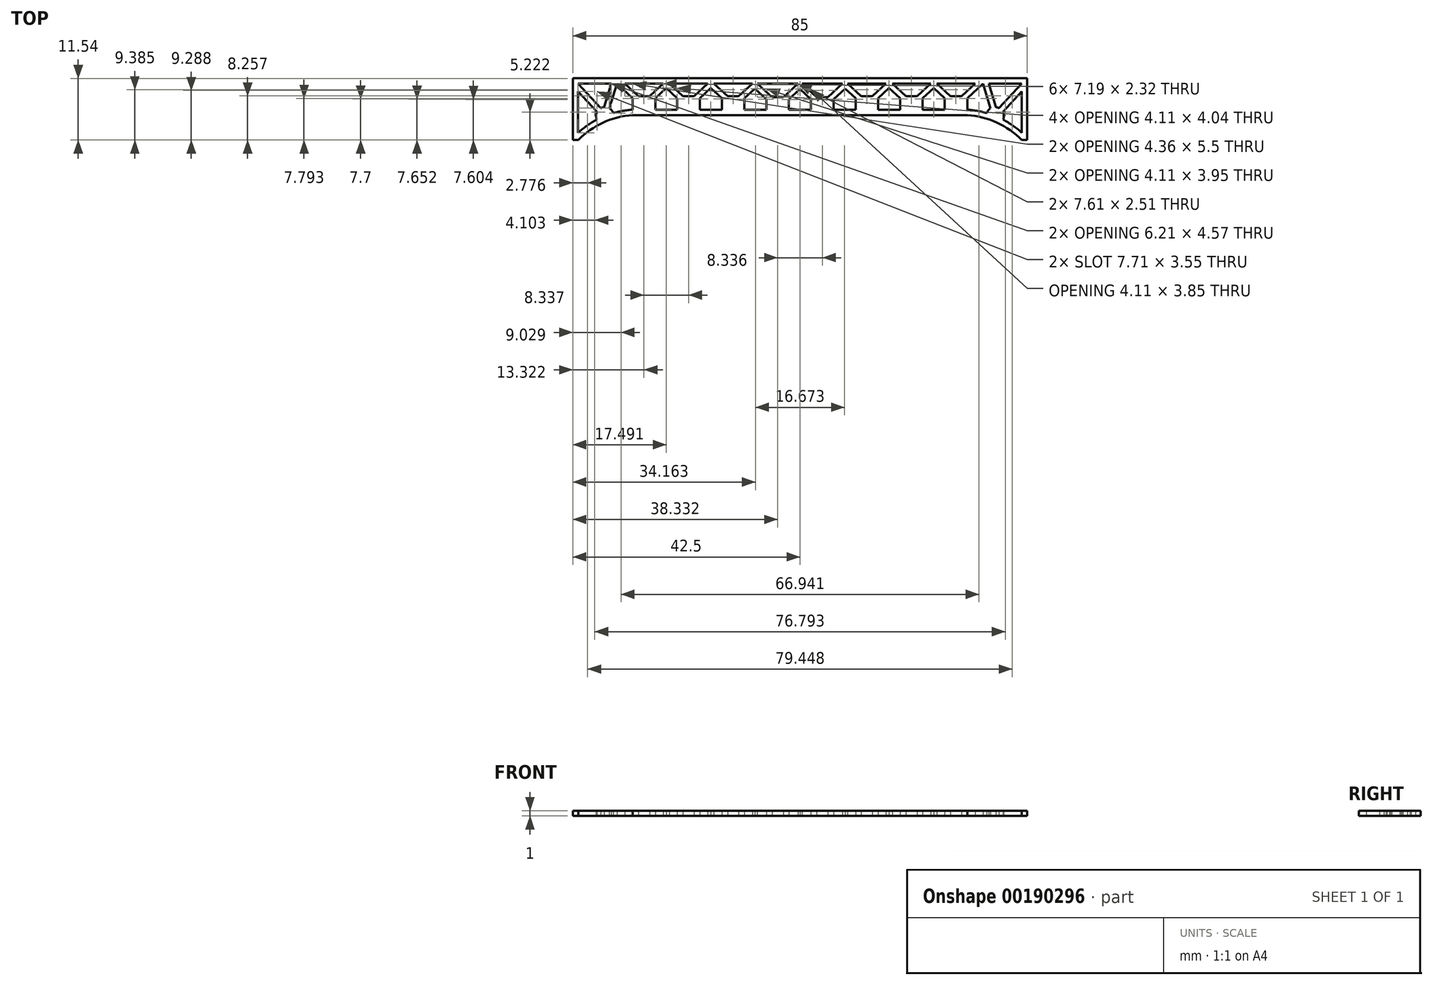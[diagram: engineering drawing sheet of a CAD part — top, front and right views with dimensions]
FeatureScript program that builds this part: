
annotation { "Feature Type Name" : "Feature", "Feature Type Description" : "" }
export const myFeature = defineFeature(function(context is Context, id is Id, definition is map)
    precondition{}
    {
        {
            var Q0;
            Q0=qCreatedBy(makeId("Top.planeOp"),FACE);
            var sketch = newSketch(context, id + "F0", { "sketchPlane" : qUnion([Q0])});
            skLineSegment(sketch, "E0", {"start": v(41.49, -5.77) * mm, "end": v(42.5, -5.77) * mm});
            skLineSegment(sketch, "E1", {"start": v(-28.13, 2.46) * mm, "end": v(-30.22, 2.46) * mm});
            skLineSegment(sketch, "E2", {"start": v(-31.29, -0.1) * mm, "end": v(-31.29, 2.08) * mm});
            skArc(sketch, "E3", {"start": v(41.49, -5.77) * mm, "mid": v(36.82, -2.5) * mm, "end": v(31.29, -1.1) * mm});
            skLineSegment(sketch, "E4", {"start": v(42.5, -5.77) * mm, "end": v(42.5, 5.77) * mm});
            skLineSegment(sketch, "E5", {"start": v(-30.22, 2.46) * mm, "end": v(-32.77, 4.77) * mm});
            skLineSegment(sketch, "E6", {"start": v(-42.5, -5.77) * mm, "end": v(-42.5, 5.77) * mm});
            skArc(sketch, "E7", {"start": v(-31.29, -1.1) * mm, "mid": v(-36.82, -2.5) * mm, "end": v(-41.49, -5.77) * mm});
            skLineSegment(sketch, "E8", {"start": v(-41.49, -5.77) * mm, "end": v(-42.5, -5.77) * mm});
            skLineSegment(sketch, "E9", {"start": v(-42.5, 5.77) * mm, "end": v(42.5, 5.77) * mm});
            skLineSegment(sketch, "E10", {"start": v(-31.29, -1.1) * mm, "end": v(31.29, -1.1) * mm});
            skLineSegment(sketch, "E11", {"start": v(-41.5, 4.77) * mm, "end": v(-35.3, 4.77) * mm});
            skLineSegment(sketch, "E12", {"start": v(-41.5, -4.4) * mm, "end": v(-41.5, 3.3) * mm});
            skArc(sketch, "E13", {"start": v(-31.29, -0.1) * mm, "mid": v(-33.12, -0.3) * mm, "end": v(-34.92, -0.73) * mm});
            skLineSegment(sketch, "E14", {"start": v(-31.29, 2.08) * mm, "end": v(-34.25, 4.77) * mm});
            skLineSegment(sketch, "E15", {"start": v(-27.07, -0.1) * mm, "end": v(-27.07, 2.08) * mm});
            skLineSegment(sketch, "E16", {"start": v(-28.13, 2.46) * mm, "end": v(-25.58, 4.77) * mm});
            skLineSegment(sketch, "E17", {"start": v(-27.07, 2.08) * mm, "end": v(-25, 3.95) * mm});
            skLineSegment(sketch, "E18", {"start": v(-21.89, 2.46) * mm, "end": v(-24.43, 4.77) * mm});
            skLineSegment(sketch, "E19", {"start": v(-18.73, -0.1) * mm, "end": v(-18.73, 2.08) * mm});
            skLineSegment(sketch, "E20", {"start": v(-19.8, 2.46) * mm, "end": v(-21.89, 2.46) * mm});
            skLineSegment(sketch, "E21", {"start": v(-22.95, -0.1) * mm, "end": v(-22.95, 2.08) * mm});
            skLineSegment(sketch, "E22", {"start": v(-19.8, 2.46) * mm, "end": v(-17.25, 4.77) * mm});
            skLineSegment(sketch, "E23", {"start": v(-18.73, 2.08) * mm, "end": v(-16.67, 3.95) * mm});
            skLineSegment(sketch, "E24", {"start": v(-22.95, 2.08) * mm, "end": v(-25, 3.95) * mm});
            skLineSegment(sketch, "E25", {"start": v(-13.55, 2.46) * mm, "end": v(-16.1, 4.77) * mm});
            skLineSegment(sketch, "E26", {"start": v(-10.4, -0.1) * mm, "end": v(-10.4, 2.08) * mm});
            skLineSegment(sketch, "E27", {"start": v(-11.46, 2.46) * mm, "end": v(-13.55, 2.46) * mm});
            skLineSegment(sketch, "E28", {"start": v(-14.62, -0.1) * mm, "end": v(-14.62, 2.08) * mm});
            skLineSegment(sketch, "E29", {"start": v(-11.46, 2.46) * mm, "end": v(-8.91, 4.77) * mm});
            skLineSegment(sketch, "E30", {"start": v(-10.4, 2.08) * mm, "end": v(-8.44, 3.85) * mm});
            skLineSegment(sketch, "E31", {"start": v(-14.62, 2.08) * mm, "end": v(-16.67, 3.95) * mm});
            skLineSegment(sketch, "E32", {"start": v(-5.22, 2.26) * mm, "end": v(-7.97, 4.77) * mm});
            skLineSegment(sketch, "E33", {"start": v(-2.06, -0.1) * mm, "end": v(-2.06, 1.88) * mm});
            skLineSegment(sketch, "E34", {"start": v(-3.12, 2.26) * mm, "end": v(-5.22, 2.26) * mm});
            skLineSegment(sketch, "E35", {"start": v(-6.28, -0.1) * mm, "end": v(-6.28, 1.88) * mm});
            skLineSegment(sketch, "E36", {"start": v(-3.12, 2.26) * mm, "end": v(-0.36, 4.77) * mm});
            skLineSegment(sketch, "E37", {"start": v(-2.06, 1.88) * mm, "end": v(0, 3.76) * mm});
            skLineSegment(sketch, "E38", {"start": v(-6.28, 1.88) * mm, "end": v(-8.44, 3.85) * mm});
            skLineSegment(sketch, "E39", {"start": v(-32.77, 4.77) * mm, "end": v(-25.58, 4.77) * mm});
            skLineSegment(sketch, "E40", {"start": v(-24.43, 4.77) * mm, "end": v(-17.25, 4.77) * mm});
            skLineSegment(sketch, "E41", {"start": v(-16.1, 4.77) * mm, "end": v(-8.91, 4.77) * mm});
            skLineSegment(sketch, "E42", {"start": v(-7.97, 4.77) * mm, "end": v(-0.36, 4.77) * mm});
            skLineSegment(sketch, "E43", {"start": v(-27.07, -0.1) * mm, "end": v(-22.95, -0.1) * mm});
            skLineSegment(sketch, "E44", {"start": v(-18.73, -0.1) * mm, "end": v(-14.62, -0.1) * mm});
            skLineSegment(sketch, "E45", {"start": v(-10.4, -0.1) * mm, "end": v(-6.28, -0.1) * mm});
            skLineSegment(sketch, "E46", {"start": v(-2.06, -0.1) * mm, "end": v(0, -0.1) * mm});
            skLineSegment(sketch, "E47", {"start": v(-35.65, 0.16) * mm, "end": v(-34.25, 4.77) * mm});
            skLineSegment(sketch, "E48", {"start": v(-36.63, 0.38) * mm, "end": v(-35.3, 4.77) * mm});
            skLineSegment(sketch, "E49", {"start": v(-37.24, 0.2) * mm, "end": v(-41.5, 4.77) * mm});
            skLineSegment(sketch, "E50", {"start": v(-37.95, -0.5) * mm, "end": v(-41.5, 3.3) * mm});
            skArc(sketch, "E51", {"start": v(-34.92, -0.73) * mm, "mid": v(-35.2, -0.22) * mm, "end": v(-35.65, 0.16) * mm});
            skArc(sketch, "E52", {"start": v(-37.98, -1.96) * mm, "mid": v(-39.82, -3.07) * mm, "end": v(-41.5, -4.4) * mm});
            skLineSegment(sketch, "E53", {"start": v(30.22, 2.46) * mm, "end": v(32.77, 4.77) * mm});
            skLineSegment(sketch, "E54", {"start": v(41.5, -4.4) * mm, "end": v(41.5, 3.3) * mm});
            skLineSegment(sketch, "E55", {"start": v(31.29, 2.08) * mm, "end": v(34.25, 4.77) * mm});
            skLineSegment(sketch, "E56", {"start": v(27.07, -0.1) * mm, "end": v(27.07, 2.08) * mm});
            skLineSegment(sketch, "E57", {"start": v(28.13, 2.46) * mm, "end": v(30.22, 2.46) * mm});
            skLineSegment(sketch, "E58", {"start": v(31.29, -0.1) * mm, "end": v(31.29, 2.08) * mm});
            skLineSegment(sketch, "E59", {"start": v(28.13, 2.46) * mm, "end": v(25.58, 4.77) * mm});
            skLineSegment(sketch, "E60", {"start": v(27.07, 2.08) * mm, "end": v(25, 3.95) * mm});
            skLineSegment(sketch, "E61", {"start": v(21.89, 2.46) * mm, "end": v(24.43, 4.77) * mm});
            skLineSegment(sketch, "E62", {"start": v(18.73, -0.1) * mm, "end": v(18.73, 2.08) * mm});
            skLineSegment(sketch, "E63", {"start": v(19.8, 2.46) * mm, "end": v(21.89, 2.46) * mm});
            skLineSegment(sketch, "E64", {"start": v(22.95, -0.1) * mm, "end": v(22.95, 2.08) * mm});
            skLineSegment(sketch, "E65", {"start": v(19.8, 2.46) * mm, "end": v(17.25, 4.77) * mm});
            skLineSegment(sketch, "E66", {"start": v(18.73, 2.08) * mm, "end": v(16.67, 3.95) * mm});
            skLineSegment(sketch, "E67", {"start": v(22.95, 2.08) * mm, "end": v(25, 3.95) * mm});
            skLineSegment(sketch, "E68", {"start": v(13.55, 2.46) * mm, "end": v(16.1, 4.77) * mm});
            skLineSegment(sketch, "E69", {"start": v(10.4, -0.1) * mm, "end": v(10.4, 2.08) * mm});
            skLineSegment(sketch, "E70", {"start": v(11.46, 2.46) * mm, "end": v(13.55, 2.46) * mm});
            skLineSegment(sketch, "E71", {"start": v(14.62, -0.1) * mm, "end": v(14.62, 2.08) * mm});
            skLineSegment(sketch, "E72", {"start": v(11.46, 2.46) * mm, "end": v(8.91, 4.77) * mm});
            skLineSegment(sketch, "E73", {"start": v(10.4, 2.08) * mm, "end": v(8.44, 3.85) * mm});
            skLineSegment(sketch, "E74", {"start": v(14.62, 2.08) * mm, "end": v(16.67, 3.95) * mm});
            skLineSegment(sketch, "E75", {"start": v(5.22, 2.26) * mm, "end": v(7.97, 4.77) * mm});
            skLineSegment(sketch, "E76", {"start": v(2.06, -0.1) * mm, "end": v(2.06, 1.88) * mm});
            skLineSegment(sketch, "E77", {"start": v(3.12, 2.26) * mm, "end": v(5.22, 2.26) * mm});
            skLineSegment(sketch, "E78", {"start": v(6.28, -0.1) * mm, "end": v(6.28, 1.88) * mm});
            skLineSegment(sketch, "E79", {"start": v(3.12, 2.26) * mm, "end": v(0.36, 4.77) * mm});
            skLineSegment(sketch, "E80", {"start": v(6.28, 1.88) * mm, "end": v(8.44, 3.85) * mm});
            skLineSegment(sketch, "E81", {"start": v(2.06, 1.88) * mm, "end": v(0, 3.76) * mm});
            skLineSegment(sketch, "E82", {"start": v(32.77, 4.77) * mm, "end": v(25.58, 4.77) * mm});
            skLineSegment(sketch, "E83", {"start": v(24.43, 4.77) * mm, "end": v(17.25, 4.77) * mm});
            skLineSegment(sketch, "E84", {"start": v(16.1, 4.77) * mm, "end": v(8.91, 4.77) * mm});
            skLineSegment(sketch, "E85", {"start": v(27.07, -0.1) * mm, "end": v(22.95, -0.1) * mm});
            skLineSegment(sketch, "E86", {"start": v(18.73, -0.1) * mm, "end": v(14.62, -0.1) * mm});
            skLineSegment(sketch, "E87", {"start": v(2.06, -0.1) * mm, "end": v(0, -0.1) * mm});
            skLineSegment(sketch, "E88", {"start": v(10.4, -0.1) * mm, "end": v(6.28, -0.1) * mm});
            skLineSegment(sketch, "E89", {"start": v(41.5, 4.77) * mm, "end": v(35.3, 4.77) * mm});
            skArc(sketch, "E90", {"start": v(37.98, -1.96) * mm, "mid": v(38.13, -1.23) * mm, "end": v(37.95, -0.5) * mm});
            skArc(sketch, "E91", {"start": v(41.5, -4.4) * mm, "mid": v(39.82, -3.07) * mm, "end": v(37.98, -1.96) * mm});
            skArc(sketch, "E92", {"start": v(34.92, -0.73) * mm, "mid": v(33.12, -0.3) * mm, "end": v(31.29, -0.1) * mm});
            skLineSegment(sketch, "E93", {"start": v(35.65, 0.16) * mm, "end": v(34.25, 4.77) * mm});
            skLineSegment(sketch, "E94", {"start": v(37.95, -0.5) * mm, "end": v(41.5, 3.3) * mm});
            skLineSegment(sketch, "E95", {"start": v(36.63, 0.38) * mm, "end": v(35.3, 4.77) * mm});
            skLineSegment(sketch, "E96", {"start": v(37.24, 0.2) * mm, "end": v(41.5, 4.77) * mm});
            skLineSegment(sketch, "E97", {"start": v(7.97, 4.77) * mm, "end": v(0.36, 4.77) * mm});
            skArc(sketch, "E98", {"start": v(-37.95, -0.5) * mm, "mid": v(-38.13, -1.23) * mm, "end": v(-37.98, -1.96) * mm});
            skArc(sketch, "E99", {"start": v(-36.63, 0.38) * mm, "mid": v(-36.94, 0.32) * mm, "end": v(-37.24, 0.2) * mm});
            skArc(sketch, "E100", {"start": v(35.65, 0.16) * mm, "mid": v(35.2, -0.22) * mm, "end": v(34.92, -0.73) * mm});
            skArc(sketch, "E101", {"start": v(37.24, 0.2) * mm, "mid": v(36.94, 0.32) * mm, "end": v(36.63, 0.38) * mm});
            skSolve(sketch);
        }
        {
            var Q0;
            Q0 = qSketchRegion(id + "F0", true);
            extrude(context, id + "F1", {"entities" : qUnion([Q0]), "depth" : 1 * mm});
        }
    });
